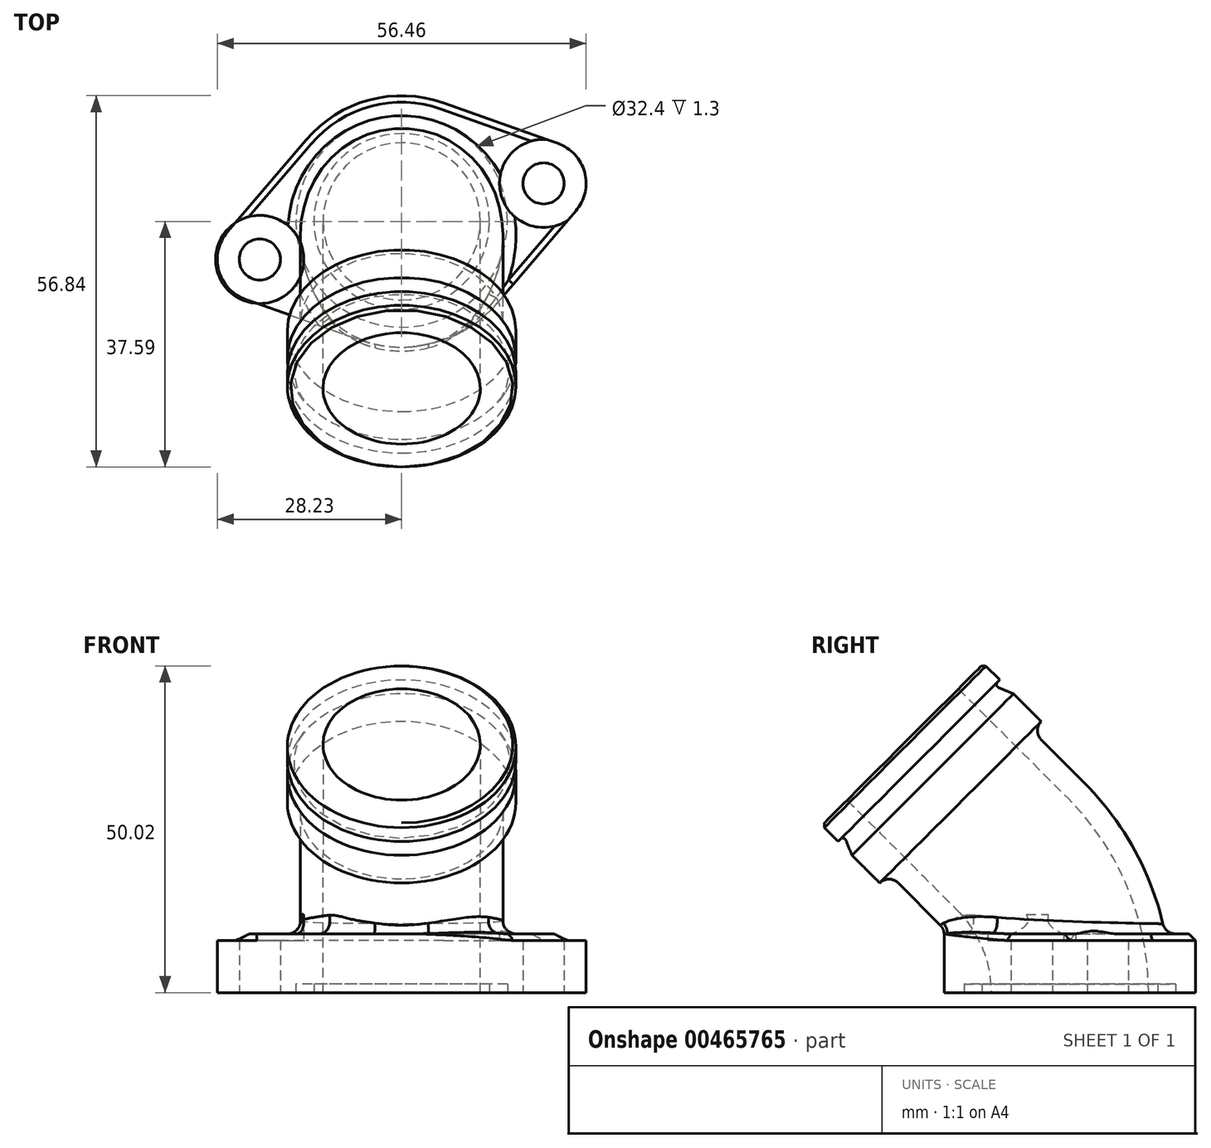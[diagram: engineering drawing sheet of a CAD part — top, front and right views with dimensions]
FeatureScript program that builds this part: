
annotation { "Feature Type Name" : "Feature", "Feature Type Description" : "" }
export const myFeature = defineFeature(function(context is Context, id is Id, definition is map)
    precondition{}
    {
        {
            var Q0;
            Q0=qCreatedBy(makeId("Top.planeOp"),FACE);
            var sketch = newSketch(context, id + "F0", { "sketchPlane" : qUnion([Q0])});
            skCircle(sketch, "E0", {"center": v(0, 0) * mm, "radius": 12.25 * mm, "construction": true});
            skCircle(sketch, "E1", {"center": v(0, 0) * mm, "radius": 22.5 * mm, "construction": true});
            skPoint(sketch, "E2", {"position": v(22.5, 0) * mm});
            skPoint(sketch, "E3", {"position": v(-22.5, 0) * mm});
            skArc(sketch, "E4", {"start": v(6.43, 18.14) * mm, "mid": v(-4.98, 18.6) * mm, "end": v(-14.64, 12.5) * mm});
            skLineSegment(sketch, "E5", {"start": v(6.43, 18.14) * mm, "end": v(23.9, 11.95) * mm});
            skLineSegment(sketch, "E6", {"start": v(26.68, 1.6) * mm, "end": v(14.64, -12.5) * mm});
            skLineSegment(sketch, "E7", {"start": v(-23.9, -11.95) * mm, "end": v(-6.43, -18.14) * mm});
            skLineSegment(sketch, "E8", {"start": v(-26.68, -1.6) * mm, "end": v(-14.64, 12.5) * mm});
            skLineSegment(sketch, "E9", {"start": v(0, 0) * mm, "end": v(0, 0) * mm});
            skArc(sketch, "E10.trimOffspring", {"start": v(-6.43, -18.14) * mm, "mid": v(4.98, -18.6) * mm, "end": v(14.64, -12.5) * mm});
            skLineSegment(sketch, "E11", {"start": v(0, 0) * mm, "end": v(37.9, 0) * mm, "construction": true});
            skArc(sketch, "E12", {"start": v(26.68, 1.6) * mm, "mid": v(28.01, 7.5) * mm, "end": v(23.9, 11.95) * mm});
            skArc(sketch, "E13", {"start": v(-26.68, -1.6) * mm, "mid": v(-28.01, -7.5) * mm, "end": v(-23.9, -11.95) * mm});
            skLineSegment(sketch, "E14", {"start": v(0, 0) * mm, "end": v(21.73, 5.82) * mm, "construction": true});
            skSolve(sketch);
        }
        {
            var Q0;
            Q0 = qSketchRegion(id + "F0", true);
            extrude(context, id + "F1", {"entities" : qUnion([Q0]), "depth" : 9 * mm});
        }
        {
            var Q0;
            Q0=qCreatedBy(makeId("Right.planeOp"),FACE);
            var sketch = newSketch(context, id + "F2", { "sketchPlane" : qUnion([Q0])});
            skArc(sketch, "E15", {"start": v(0, 0) * mm, "mid": v(-2.28, 11.48) * mm, "end": v(-8.79, 21.21) * mm});
            skLineSegment(sketch, "E16", {"start": v(-8.79, 21.21) * mm, "end": v(-25.57, 38) * mm});
            skSolve(sketch);
        }
        {
            var Q0;
            Q0=sQuery(id+"F2.wireOp",VERTEX,"E16.end");
            var Q1;
            Q1=sQuery(id+"F2.wireOp",EDGE,"E16");
            cPlane(context, id + "F3", {"entities" : qUnion([Q0, Q1]), "cplaneType" : CPlaneType.LINE_POINT, "offset" : 25 * mm, "width" : 150 * mm, "height" : 150 * mm});
        }
        {
            var Q0;
            Q0=qCreatedBy(id+"F3.planeOp",FACE);
            var sketch = newSketch(context, id + "F4", { "sketchPlane" : qUnion([Q0])});
            skCircle(sketch, "E17", {"center": v(0, 8.79) * mm, "radius": 15.5 * mm});
            skSolve(sketch);
        }
        {
            var Q0;
            Q0 = qSketchRegion(id + "F4", true);
            var Q1;
            Q1 = qConstructionFilter(qBodyType(qCreatedBy(id + "F2" ,EDGE), BodyType.WIRE), ConstructionObject.NO);
            sweep(context, id + "F5", {"operationType" : NewBodyOperationType.ADD, "profiles" : qUnion([Q0]), "path" : qUnion([Q1])});
        }
        {
            var Q0;
            Q0=qCreatedBy(id+"F3.planeOp",FACE);
            var sketch = newSketch(context, id + "F6", { "sketchPlane" : qUnion([Q0])});
            skCircle(sketch, "E18", {"center": v(0, 8.79) * mm, "radius": 17.5 * mm});
            skSolve(sketch);
        }
        {
            var Q0;
            Q0 = qSketchRegion(id + "F6", true);
            extrude(context, id + "F7", {"entities" : qUnion([Q0]), "operationType" : NewBodyOperationType.ADD, "oppositeDirection" : true, "depth" : 12.5 * mm});
        }
        {
            var Q0;
            Q0=qCreatedBy(makeId("Right.planeOp"),FACE);
            var sketch = newSketch(context, id + "F8", { "sketchPlane" : qUnion([Q0])});
            skArc(sketch, "E19", {"start": v(-11.08, 47.55) * mm, "mid": v(-11.21, 47.1) * mm, "end": v(-10.91, 46.73) * mm});
            skLineSegment(sketch, "E20", {"start": v(-10.91, 46.73) * mm, "end": v(-8.6, 45.78) * mm});
            skLineSegment(sketch, "E21", {"start": v(-8.6, 45.78) * mm, "end": v(-10.72, 47.9) * mm});
            skLineSegment(sketch, "E22", {"start": v(23.82, -11.4) * mm, "end": v(-48.99, 61.41) * mm, "construction": true});
            skLineSegment(sketch, "E23", {"start": v(-16.95, 54.13) * mm, "end": v(-7.13, 44.3) * mm, "construction": true});
            skLineSegment(sketch, "E24", {"start": v(-10.72, 47.9) * mm, "end": v(-11.08, 47.55) * mm});
            skSolve(sketch);
        }
        {
            var Q0;
            Q0 = qSketchRegion(id + "F8", true);
            var Q1;
            Q1=sQuery(id+"F8.wireOp",EDGE,"E22");
            revolve(context, id + "F9", {"operationType" : NewBodyOperationType.REMOVE, "entities" : qUnion([Q0]), "axis" : qUnion([Q1]), "revolveType" : RevolveType.FULL, "oppositeDirection" : true});
        }
        {
            var Q0;
            Q0=makeQuery(id+"F7.boolean.opBoolean","MERGE",FACE,{"derivedFrom":[makeQuery(id+"F5.opSweep","CAP_FACE",FACE,{"disambiguationData":[OSD([sQuery(id+"F2.wireOp",VERTEX,"E16.end"),sQuery(id+"F4.wireOp",EDGE,"E17")])],"isStart":true}),makeQuery(id+"F7.opExtrude","CAP_FACE",FACE,{"disambiguationData":[OSD([sQuery(id+"F6.wireOp",EDGE,"E18")])],"isStart":true})]});
            var sketch = newSketch(context, id + "F10", { "sketchPlane" : qUnion([Q0])});
            skCircle(sketch, "E25", {"center": v(0, 8.79) * mm, "radius": 12.05 * mm});
            skSolve(sketch);
        }
        {
            var Q0;
            Q0=makeQuery(id+"F10.imprint","IMPRINT",FACE,{"disambiguationData":[TD([[makeQuery(id+"F10.imprint","IMPRINT",EDGE,{"derivedFrom":sQuery(id+"F10.wireOp",EDGE,"E25")}),1.0]])]});
            var Q1;
            Q1=sQuery(id+"F2.wireOp",EDGE,"E16");
            var Q2;
            Q2=sQuery(id+"F2.wireOp",EDGE,"E15");
            sweep(context, id + "F11", {"operationType" : NewBodyOperationType.REMOVE, "profiles" : qUnion([Q0]), "path" : qUnion([Q1, Q2])});
        }
        {
            var Q0;
            Q0=makeQuery(id+"F7.opExtrude","CAP_EDGE",EDGE,{"disambiguationData":[OSD([sQuery(id+"F6.wireOp",EDGE,"E18")])],"isStart":true});
            chamfer(context, id + "F12", {"entities" : qUnion([Q0]), "width" : 0.5 * mm, "tangentPropagation" : true});
        }
        {
            var Q0;
            Q0=makeQuery(id+"F7.boolean.opBoolean","INTERSECT",EDGE,{"derivedFrom":[makeQuery(id+"F5.opSweep","SWEPT_FACE",FACE,{"disambiguationData":[OSD([sQuery(id+"F2.wireOp",EDGE,"E16"),sQuery(id+"F4.wireOp",EDGE,"E17")])]}),makeQuery(id+"F7.opExtrude","CAP_FACE",FACE,{"disambiguationData":[OSD([sQuery(id+"F6.wireOp",EDGE,"E18")])],"isStart":false})]});
            fillet(context, id + "F13", {"entities" : qUnion([Q0]), "radius" : 2 * mm, "tangentPropagation" : true, "allowEdgeOverflow" : false});
        }
        {
            var Q0;
            Q0=makeQuery(id+"F5.boolean.opBoolean","INTERSECT",EDGE,{"derivedFrom":[makeQuery(id+"F1.opExtrude","CAP_FACE",FACE,{"disambiguationData":[OSD([sQuery(id+"F0.wireOp",EDGE,"K1aCBvVd-vCZX-3cmT-E5vM-9w0kNDY8bLsZ"),sQuery(id+"F0.wireOp",EDGE,"dq006SXK-7DoR-124d-AdU2-wejQHuEkYCIk"),sQuery(id+"F0.wireOp",EDGE,"E4"),sQuery(id+"F0.wireOp",EDGE,"E5"),sQuery(id+"F0.wireOp",EDGE,"E6"),sQuery(id+"F0.wireOp",EDGE,"E7"),sQuery(id+"F0.wireOp",EDGE,"E8"),sQuery(id+"F0.wireOp",EDGE,"E10.trimOffspring")])],"isStart":false}),makeQuery(id+"F5.opSweep","SWEPT_FACE",FACE,{"disambiguationData":[OSD([sQuery(id+"F2.wireOp",EDGE,"E15"),sQuery(id+"F4.wireOp",EDGE,"E17")])]})]});
            fillet(context, id + "F14", {"entities" : qUnion([Q0]), "radius" : 2 * mm, "tangentPropagation" : true, "allowEdgeOverflow" : false});
        }
        {
            var Q0;
            Q0=qCreatedBy(makeId("Top.planeOp"),FACE);
            var sketch = newSketch(context, id + "F15", { "sketchPlane" : qUnion([Q0])});
            skLineSegment(sketch, "E26", {"start": v(0, 0) * mm, "end": v(21.73, 5.82) * mm, "construction": true});
            skCircle(sketch, "E27", {"center": v(21.73, 5.82) * mm, "radius": 3.15 * mm});
            skCircle(sketch, "E28", {"center": v(-21.73, -5.82) * mm, "radius": 3.15 * mm});
            skSolve(sketch);
        }
        {
            var Q0;
            Q0 = qSketchRegion(id + "F15", true);
            extrude(context, id + "F16", {"entities" : qUnion([Q0]), "operationType" : NewBodyOperationType.REMOVE, "endBound" : BoundingType.UP_TO_NEXT, "depth" : 25 * mm});
        }
        {
            var Q0;
            Q0=makeQuery(id+"F1.opExtrude","CAP_FACE",FACE,{"disambiguationData":[OSD([sQuery(id+"F0.wireOp",EDGE,"E4"),sQuery(id+"F0.wireOp",EDGE,"E5"),sQuery(id+"F0.wireOp",EDGE,"E6"),sQuery(id+"F0.wireOp",EDGE,"E7"),sQuery(id+"F0.wireOp",EDGE,"E8"),sQuery(id+"F0.wireOp",EDGE,"E10.trimOffspring"),sQuery(id+"F0.wireOp",EDGE,"igwkUbNN-ZQdT-L8VY-NQM6-FOgyPUn53SY1"),sQuery(id+"F0.wireOp",EDGE,"dd092288-4736-4224-a1c4-d597d9c2bb30.trimOffspring")])],"isStart":false});
            var sketch = newSketch(context, id + "F17", { "sketchPlane" : qUnion([Q0])});
            skCircle(sketch, "E29", {"center": v(21.73, 5.82) * mm, "radius": 6.75 * mm});
            skCircle(sketch, "E30", {"center": v(-21.73, -5.82) * mm, "radius": 6.75 * mm});
            skSolve(sketch);
        }
        {
            var Q0;
            Q0 = qSketchRegion(id + "F17", true);
            extrude(context, id + "F18", {"entities" : qUnion([Q0]), "operationType" : NewBodyOperationType.REMOVE, "depth" : 3 * mm, "hasSecondDirection" : true, "secondDirectionOppositeDirection" : true, "secondDirectionDepth" : 1 * mm});
        }
        {
            var Q0;
            Q0=makeQuery(id+"F0.imprint","IMPRINT",FACE,{"disambiguationData":[TD([[makeQuery(id+"F0.imprint","IMPRINT",EDGE,{"derivedFrom":sQuery(id+"F0.wireOp",EDGE,"E4")}),1.0]])]});
            var sketch = newSketch(context, id + "F19", { "sketchPlane" : qUnion([Q0])});
            skCircle(sketch, "E31", {"center": v(0, 0) * mm, "radius": 16.2 * mm});
            skCircle(sketch, "E32", {"center": v(0, 0) * mm, "radius": 13.45 * mm});
            skSolve(sketch);
        }
        {
            var Q0;
            Q0 = qSketchRegion(id + "F19", true);
            extrude(context, id + "F20", {"entities" : qUnion([Q0]), "operationType" : NewBodyOperationType.REMOVE, "depth" : 1.3 * mm});
        }
        {
            var Q0;
            Q0=makeQuery(id+"F1.opExtrude","CAP_EDGE",EDGE,{"disambiguationData":[OSD([sQuery(id+"F0.wireOp",EDGE,"E6")])],"isStart":false});
            var Q1;
            Q1=makeQuery(id+"F1.opExtrude","CAP_EDGE",EDGE,{"disambiguationData":[OSD([sQuery(id+"F0.wireOp",EDGE,"E5")])],"isStart":false});
            chamfer(context, id + "F21", {"entities" : qUnion([Q0, Q1]), "width" : 1 * mm, "tangentPropagation" : true});
        }
    });
